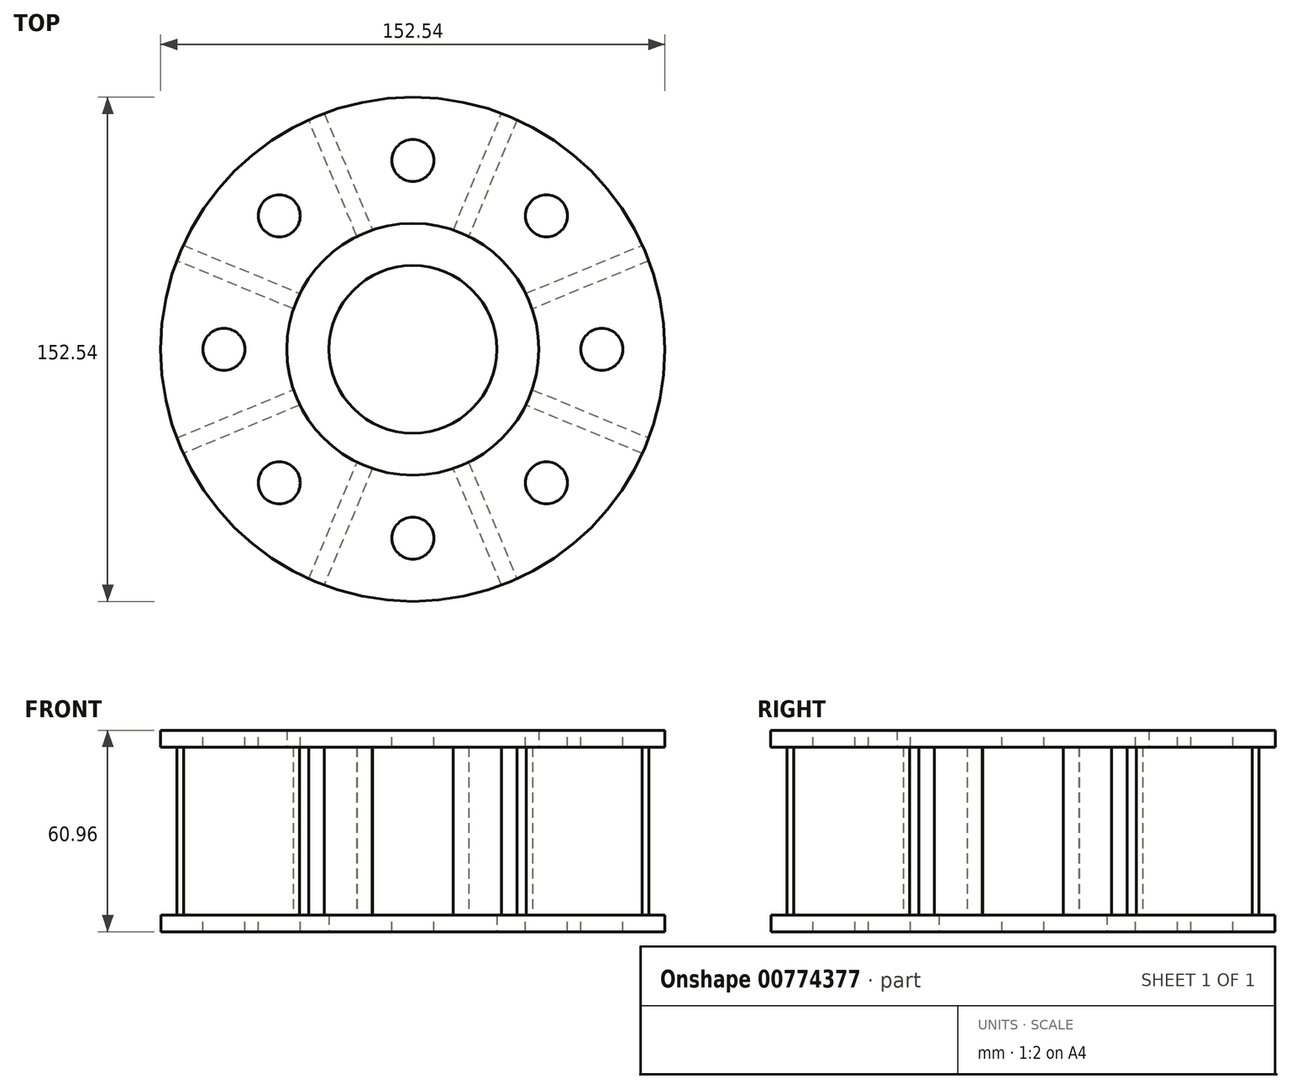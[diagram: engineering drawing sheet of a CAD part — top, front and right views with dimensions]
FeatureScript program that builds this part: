
annotation { "Feature Type Name" : "Feature", "Feature Type Description" : "" }
export const myFeature = defineFeature(function(context is Context, id is Id, definition is map)
    precondition{}
    {
        {
            var Q0;
            Q0=qCreatedBy(makeId("Top.planeOp"),FACE);
            var sketch = newSketch(context, id + "F0", { "sketchPlane" : qUnion([Q0])});
            skCircle(sketch, "E0", {"center": v(0, 0) * mm, "radius": 25.4 * mm});
            skCircle(sketch, "E1", {"center": v(0, 0) * mm, "radius": 76.2 * mm});
            skSolve(sketch);
        }
        {
            var Q0;
            Q0=makeQuery(id+"F0.imprint","IMPRINT",FACE,{"disambiguationData":[TD([[makeQuery(id+"F0.imprint","IMPRINT",EDGE,{"derivedFrom":sQuery(id+"F0.wireOp",EDGE,"E0")}),-1.0]])]});
            extrude(context, id + "F1", {"entities" : qUnion([Q0]), "depth" : 5.08 * mm, "offsetDistance" : 25.4 * mm});
        }
        {
            var Q0;
            Q0=makeQuery(id+"F1.opExtrude","CAP_FACE",FACE,{"disambiguationData":[OSD([sQuery(id+"F0.wireOp",EDGE,"E0"),sQuery(id+"F0.wireOp",EDGE,"E1")])],"isStart":false});
            cPlane(context, id + "F2", {"entities" : qUnion([Q0]), "cplaneType" : CPlaneType.OFFSET, "offset" : 50.8 * mm, "width" : 152.4 * mm, "height" : 152.4 * mm});
        }
        {
            var Q0;
            Q0=qCreatedBy(id+"F2.planeOp",FACE);
            var sketch = newSketch(context, id + "F3", { "sketchPlane" : qUnion([Q0])});
            skCircle(sketch, "E2", {"center": v(0, 0) * mm, "radius": 38.1 * mm});
            skCircle(sketch, "E3", {"center": v(0, 0) * mm, "radius": 76.27 * mm});
            skSolve(sketch);
        }
        {
            var Q0;
            Q0=makeQuery(id+"F3.imprint","IMPRINT",FACE,{"disambiguationData":[TD([[makeQuery(id+"F3.imprint","IMPRINT",EDGE,{"derivedFrom":sQuery(id+"F3.wireOp",EDGE,"E2")}),-1.0]])]});
            extrude(context, id + "F4", {"entities" : qUnion([Q0]), "depth" : 5.08 * mm, "offsetDistance" : 25.4 * mm});
        }
        {
            var Q0;
            Q0=makeQuery(id+"F4.opExtrude","CAP_FACE",FACE,{"disambiguationData":[OSD([sQuery(id+"F3.wireOp",EDGE,"E2"),sQuery(id+"F3.wireOp",EDGE,"E3")])],"isStart":false});
            var sketch = newSketch(context, id + "F5", { "sketchPlane" : qUnion([Q0])});
            skCircle(sketch, "E4", {"center": v(57.15, 0) * mm, "radius": 6.35 * mm});
            skCircle(sketch, "E5.1.0", {"center": v(40.41, 40.41) * mm, "radius": 6.35 * mm});
            skCircle(sketch, "E5.2.0", {"center": v(0, 57.15) * mm, "radius": 6.35 * mm});
            skCircle(sketch, "E5.3.0", {"center": v(-40.41, 40.41) * mm, "radius": 6.35 * mm});
            skCircle(sketch, "E5.4.0", {"center": v(-57.15, 0) * mm, "radius": 6.35 * mm});
            skCircle(sketch, "E5.5.0", {"center": v(-40.41, -40.41) * mm, "radius": 6.35 * mm});
            skCircle(sketch, "E5.6.0", {"center": v(0, -57.15) * mm, "radius": 6.35 * mm});
            skCircle(sketch, "E5.7.0", {"center": v(40.41, -40.41) * mm, "radius": 6.35 * mm});
            skPoint(sketch, "E5.center", {"position": v(0, 0) * mm});
            skSolve(sketch);
        }
        {
            var Q0;
            Q0 = qSketchRegion(id + "F5", true);
            var Q1;
            Q1=makeQuery(id+"F1.opExtrude","CAP_FACE",FACE,{"disambiguationData":[OSD([sQuery(id+"F0.wireOp",EDGE,"E0"),sQuery(id+"F0.wireOp",EDGE,"E1")])],"isStart":true});
            var Q2;
            Q2=makeQuery(id+"F1.opExtrude","SWEPT_FACE",FACE,{"disambiguationData":[OSD([sQuery(id+"F0.wireOp",EDGE,"E1")])]});
            extrude(context, id + "F6", {"entities" : qUnion([Q0, Q1]), "operationType" : NewBodyOperationType.REMOVE, "endBound" : BoundingType.THROUGH_ALL, "oppositeDirection" : true, "depth" : 2540 * mm, "endBoundEntityFace" : qUnion([Q2]), "offsetDistance" : 25.4 * mm});
        }
        {
            var Q0;
            Q0=makeQuery(id+"F1.opExtrude","CAP_FACE",FACE,{"disambiguationData":[OSD([sQuery(id+"F0.wireOp",EDGE,"E0"),sQuery(id+"F0.wireOp",EDGE,"E1")])],"isStart":false});
            var sketch = newSketch(context, id + "F7", { "sketchPlane" : qUnion([Q0])});
            skCircle(sketch, "E6", {"center": v(57.15, 0) * mm, "radius": 6.35 * mm});
            skCircle(sketch, "E7.1.0", {"center": v(40.41, 40.41) * mm, "radius": 6.35 * mm});
            skCircle(sketch, "E7.2.0", {"center": v(0, 57.15) * mm, "radius": 6.35 * mm});
            skCircle(sketch, "E7.3.0", {"center": v(-40.41, 40.41) * mm, "radius": 6.35 * mm});
            skCircle(sketch, "E7.4.0", {"center": v(-57.15, 0) * mm, "radius": 6.35 * mm});
            skCircle(sketch, "E7.5.0", {"center": v(-40.41, -40.41) * mm, "radius": 6.35 * mm});
            skCircle(sketch, "E7.6.0", {"center": v(0, -57.15) * mm, "radius": 6.35 * mm});
            skCircle(sketch, "E7.7.0", {"center": v(40.41, -40.41) * mm, "radius": 6.35 * mm});
            skPoint(sketch, "E7.center", {"position": v(0, 0) * mm});
            skSolve(sketch);
        }
        {
            var Q0;
            Q0 = qSketchRegion(id + "F7", true);
            extrude(context, id + "F8", {"entities" : qUnion([Q0]), "operationType" : NewBodyOperationType.REMOVE, "oppositeDirection" : true, "depth" : 25.4 * mm, "offsetDistance" : 25.4 * mm});
        }
        {
            var Q0;
            Q0=makeQuery(id+"F1.opExtrude","CAP_FACE",FACE,{"disambiguationData":[OSD([sQuery(id+"F0.wireOp",EDGE,"E0"),sQuery(id+"F0.wireOp",EDGE,"E1")])],"isStart":false});
            var sketch = newSketch(context, id + "F9", { "sketchPlane" : qUnion([Q0])});
            skLineSegment(sketch, "E8", {"start": v(0, 0) * mm, "end": v(28.66, -69.19) * mm});
            skLineSegment(sketch, "E9", {"start": v(16.96, -34.3) * mm, "end": v(31.5, -69.39) * mm});
            skLineSegment(sketch, "E10", {"start": v(26.8, -71.33) * mm, "end": v(12.25, -36.2) * mm});
            skLineSegment(sketch, "E11", {"start": v(12.25, -36.2) * mm, "end": v(16.96, -34.3) * mm});
            skLineSegment(sketch, "E12", {"start": v(31.5, -69.39) * mm, "end": v(26.8, -71.33) * mm});
            skSolve(sketch);
        }
        {
            var Q0;
            {var subQ1=sQuery(id+"F9.wireOp",EDGE,"E9");Q0=makeQuery(id+"F9.imprint","IMPRINT",FACE,{"disambiguationData":[TD([[makeQuery(id+"F9.imprint","IMPRINT",EDGE,{"derivedFrom":subQ1}),-1.0]])]});}
            extrude(context, id + "F10", {"entities" : qUnion([Q0]), "endBound" : BoundingType.UP_TO_NEXT, "depth" : 25.4 * mm, "offsetDistance" : 25.4 * mm});
        }
        {
            var Q0;
            Q0=makeQuery(id+"F10.opExtrude","SWEPT_BODY",BODY,{"disambiguationData":[OSD([sQuery(id+"F9.wireOp",EDGE,"E9"),sQuery(id+"F9.wireOp",EDGE,"E10"),sQuery(id+"F9.wireOp",EDGE,"E11"),sQuery(id+"F9.wireOp",EDGE,"E12")])]});
            var Q1;
            Q1=makeQuery(id+"F4.opExtrude","CAP_EDGE",EDGE,{"disambiguationData":[OSD([sQuery(id+"F3.wireOp",EDGE,"E2")])],"isStart":false});
            circularPattern(context, id + "F11", {"entities" : qUnion([Q0]), "axis" : qUnion([Q1]), "angle" : 360 * degree, "instanceCount" : 8, "equalSpace" : true});
        }
    });
